# Revit family: Folding_Shower_Dressing_Area_Seat-Bobrick-B-5193
name_source: partatom
category: Specialty Equipment
revit_build: Autodesk Revit 2018 (Build: 20170223_1515(x64)
units: mm (PartAtom-declared; Revit-internal decimal feet)

## family parameters
Cut with Voids When Loaded = No
Host = Face
OmniClass Number = 23.40.20.21
OmniClass Title = Toilet and Bath Specialties
Part Type = Normal
Room Calculation Point = No
Round Connector Dimension = Use Diameter
Shared = Yes

## types (1)
- B-5193
    ADA Compliant = Yes
    Assembly Code = E2010
    Baseplate Material = Metal-Bobrick-Stainless Steel
    Default Elevation = 0"
    Description = Solid Phenolic Folding Shower / Dressing Area Seat
    Frame Material = Stainless Steel-Bobrick-Satin
    Guide Bracket Material = Stainless Steel-Bobrick-Satin
    Height = 13 3/4"
    Installation Type = Wall Mounted
    Length = 15 13/16"
    Manufacturer = Bobrick
    Material = Fused Plastic-Bobrick-Ivory Matte
    Model = B-5193
    Mounting Flanges Material = Stainless Steel-Bobrick-Satin
    Mounting Height = 17"
    Mounting Height Constraint = 17"
    Price = Prices may vary. Please consult Manufacturer Representative for most up-to-date price list.
    Product Documentation Link = https://www.bobrick.com
    Product Page URL = https://www.bobrick.com
    Revised Date = 09/09/2021
    Seat Length = 14 7/16"
    Seat Material = Fused Plastic-Bobrick-Ivory Matte
    Spring Material = Metal-Bobrick-Stainless Steel
    Support Load = 500 lbs., (227 kg)
    Type Comments = To avoid potential seat malfunction, DO NOT use seat if weight exceeds 500 lbs (227 kg)
    URL = https://www.bobrick.com
    Warranty Documentation Link = https://www.bobrick.com
    Width = 25 1/2"

## geometry (parser evidence)
native form markers: Sweep x2
no freeform markers — native parametric forms only
